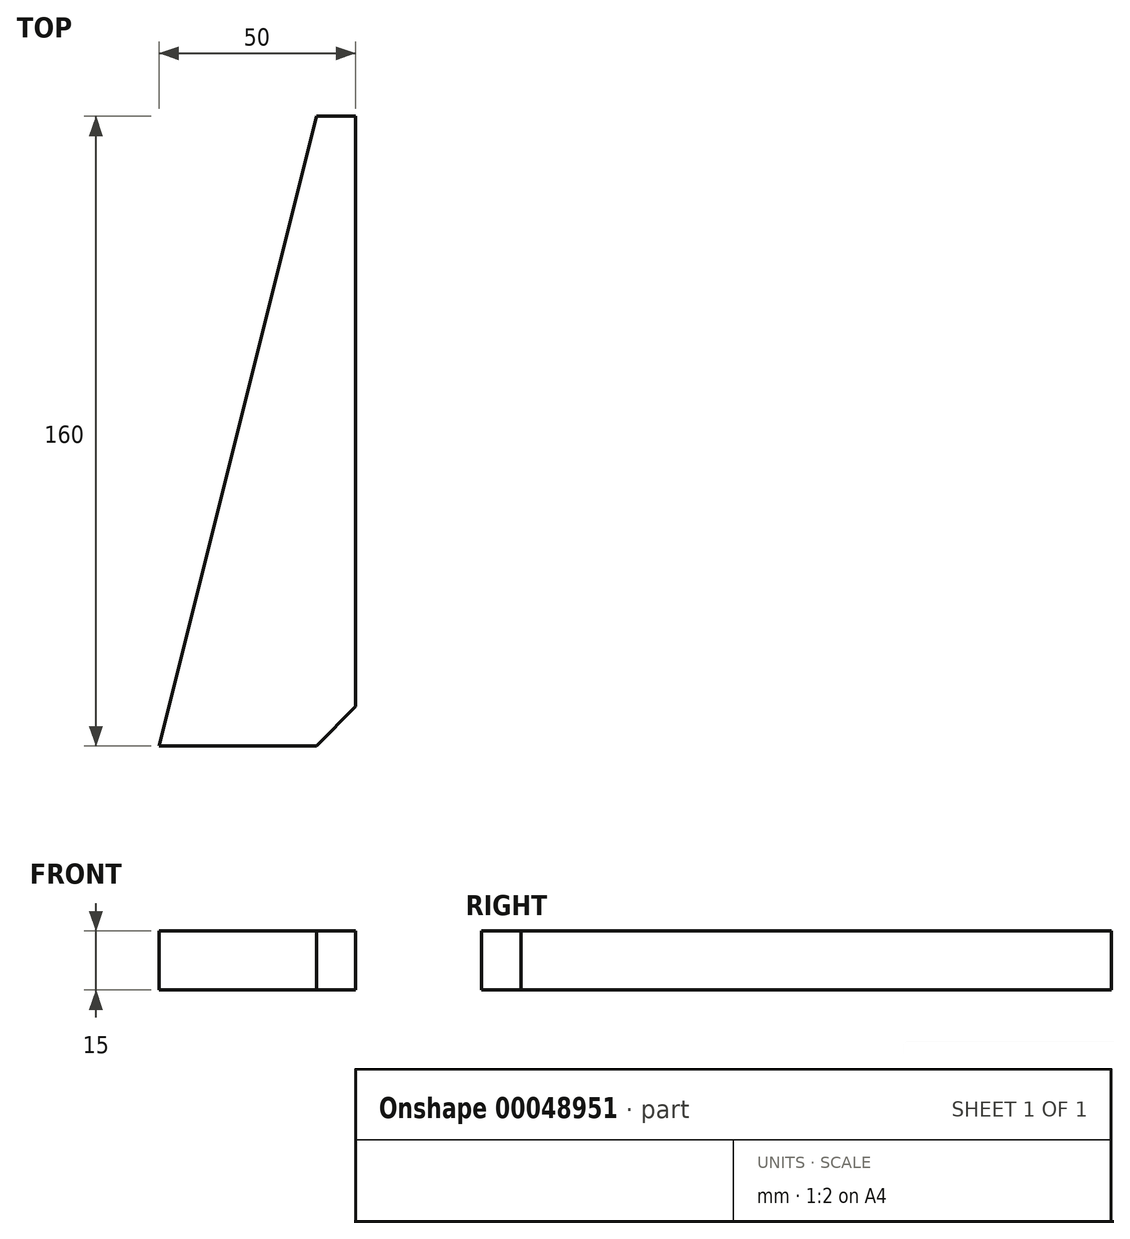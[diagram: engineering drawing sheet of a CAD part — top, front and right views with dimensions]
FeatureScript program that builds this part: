
annotation { "Feature Type Name" : "Feature", "Feature Type Description" : "" }
export const myFeature = defineFeature(function(context is Context, id is Id, definition is map)
    precondition{}
    {
        {
            var Q0;
            Q0=qCreatedBy(makeId("Top.planeOp"),FACE);
            var sketch = newSketch(context, id + "F0", { "sketchPlane" : qUnion([Q0])});
            skLineSegment(sketch, "E0.rect.bottom", {"start": v(25, 80) * mm, "end": v(-25, 80) * mm});
            skLineSegment(sketch, "E0.rect.top", {"start": v(25, -80) * mm, "end": v(-25, -80) * mm});
            skLineSegment(sketch, "E0.rect.left", {"start": v(25, 80) * mm, "end": v(25, -80) * mm});
            skLineSegment(sketch, "E0.rect.right", {"start": v(-25, 80) * mm, "end": v(-25, -80) * mm});
            skPoint(sketch, "E0.rect.middle", {"position": v(0, 0) * mm});
            skSolve(sketch);
        }
        {
            var Q0;
            Q0=makeQuery(id+"F0.imprint","IMPRINT",FACE,{"disambiguationData":[TD([[makeQuery(id+"F0.imprint","IMPRINT",EDGE,{"derivedFrom":sQuery(id+"F0.wireOp",EDGE,"E0.rect.bottom")}),1.0]])]});
            extrude(context, id + "F1", {"entities" : qUnion([Q0]), "depth" : 15 * mm});
        }
        {
            var Q0;
            Q0=makeQuery(id+"F1.opExtrude","SWEPT_EDGE",EDGE,{"disambiguationData":[OSD([sQuery(id+"F0.wireOp",EDGE,"E0.rect.bottom"),sQuery(id+"F0.wireOp",EDGE,"E0.rect.right")])]});
            chamfer(context, id + "F2", {"entities" : qUnion([Q0]), "chamferType" : ChamferType.TWO_OFFSETS, "width1" : 40 * mm, "oppositeDirection" : true, "width2" : 160 * mm, "tangentPropagation" : true});
        }
        {
            var Q0;
            Q0=makeQuery(id+"F1.opExtrude","SWEPT_EDGE",EDGE,{"disambiguationData":[OSD([sQuery(id+"F0.wireOp",EDGE,"E0.rect.top"),sQuery(id+"F0.wireOp",EDGE,"E0.rect.left")])]});
            chamfer(context, id + "F3", {"entities" : qUnion([Q0]), "chamferType" : ChamferType.OFFSET_ANGLE, "width" : 10 * mm, "oppositeDirection" : false, "angle" : 45 * degree, "tangentPropagation" : true});
        }
    });
